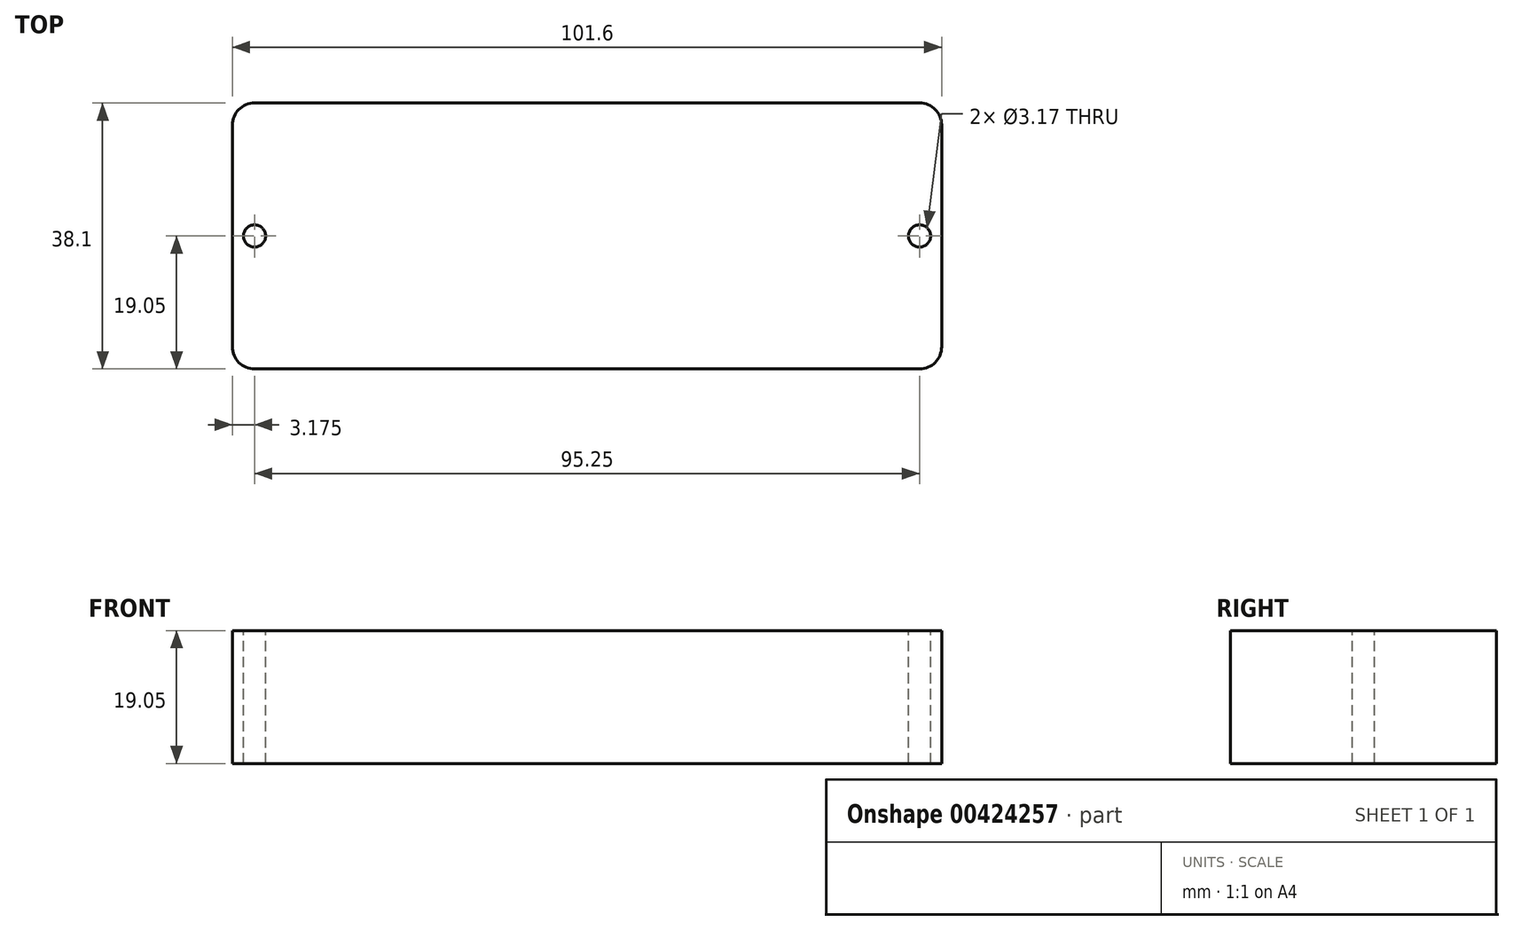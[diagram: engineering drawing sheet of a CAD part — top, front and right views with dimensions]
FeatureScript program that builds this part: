
annotation { "Feature Type Name" : "Feature", "Feature Type Description" : "" }
export const myFeature = defineFeature(function(context is Context, id is Id, definition is map)
    precondition{}
    {
        {
            var Q0;
            Q0=qCreatedBy(makeId("Top.planeOp"),FACE);
            var sketch = newSketch(context, id + "F0", { "sketchPlane" : qUnion([Q0])});
            skLineSegment(sketch, "E0.bottom", {"start": v(-50.8, -19.05) * mm, "end": v(50.8, -19.05) * mm});
            skLineSegment(sketch, "E0.top", {"start": v(-50.8, 19.05) * mm, "end": v(50.8, 19.05) * mm});
            skLineSegment(sketch, "E0.left", {"start": v(-50.8, -19.05) * mm, "end": v(-50.8, 19.05) * mm});
            skLineSegment(sketch, "E0.right", {"start": v(50.8, -19.05) * mm, "end": v(50.8, 19.05) * mm});
            skPoint(sketch, "E0.middle", {"position": v(0, 0) * mm});
            skSolve(sketch);
        }
        {
            var Q0;
            Q0=makeQuery(id+"F0.imprint","IMPRINT",FACE,{"disambiguationData":[TD([[makeQuery(id+"F0.imprint","IMPRINT",EDGE,{"derivedFrom":sQuery(id+"F0.wireOp",EDGE,"E0.bottom")}),1.0]])]});
            extrude(context, id + "F1", {"entities" : qUnion([Q0]), "depth" : 19.05 * mm});
        }
        {
            var Q0;
            Q0=makeQuery(id+"F1.opExtrude","SWEPT_EDGE",EDGE,{"disambiguationData":[OSD([sQuery(id+"F0.wireOp",EDGE,"E0.top"),sQuery(id+"F0.wireOp",EDGE,"E0.left")])]});
            var Q1;
            Q1=makeQuery(id+"F1.opExtrude","SWEPT_EDGE",EDGE,{"disambiguationData":[OSD([sQuery(id+"F0.wireOp",EDGE,"E0.bottom"),sQuery(id+"F0.wireOp",EDGE,"E0.left")])]});
            var Q2;
            Q2=makeQuery(id+"F1.opExtrude","SWEPT_EDGE",EDGE,{"disambiguationData":[OSD([sQuery(id+"F0.wireOp",EDGE,"E0.top"),sQuery(id+"F0.wireOp",EDGE,"E0.right")])]});
            var Q3;
            Q3=makeQuery(id+"F1.opExtrude","SWEPT_EDGE",EDGE,{"disambiguationData":[OSD([sQuery(id+"F0.wireOp",EDGE,"E0.bottom"),sQuery(id+"F0.wireOp",EDGE,"E0.right")])]});
            fillet(context, id + "F2", {"entities" : qUnion([Q0, Q1, Q2, Q3]), "radius" : 3.17 * mm, "tangentPropagation" : true, "allowEdgeOverflow" : false});
        }
        {
            var Q0;
            Q0=makeQuery(id+"F1.opExtrude","CAP_FACE",FACE,{"disambiguationData":[OSD([sQuery(id+"F0.wireOp",EDGE,"E0.bottom"),sQuery(id+"F0.wireOp",EDGE,"E0.top"),sQuery(id+"F0.wireOp",EDGE,"E0.left"),sQuery(id+"F0.wireOp",EDGE,"E0.right")])],"isStart":false});
            var sketch = newSketch(context, id + "F3", { "sketchPlane" : qUnion([Q0])});
            skLineSegment(sketch, "E1", {"start": v(0, 0) * mm, "end": v(-47.63, 0) * mm});
            skLineSegment(sketch, "E2", {"start": v(0, 0) * mm, "end": v(47.63, 0) * mm});
            skSolve(sketch);
        }
        {
            var Q0;
            Q0=sQuery(id+"F3.wireOp",VERTEX,"E1.end");
            var Q1;
            Q1=sQuery(id+"F3.wireOp",VERTEX,"E2.end");
            var Q2;
            Q2=makeQuery(id+"F1.opExtrude","SWEPT_BODY",BODY,{"disambiguationData":[OSD([sQuery(id+"F0.wireOp",EDGE,"E0.bottom"),sQuery(id+"F0.wireOp",EDGE,"E0.top"),sQuery(id+"F0.wireOp",EDGE,"E0.left"),sQuery(id+"F0.wireOp",EDGE,"E0.right")])]});
            hole(context, id + "F4", {"style" : HoleStyle.SIMPLE, "endStyle" : HoleEndStyle.THROUGH, "holeDiameter" : 3.17 * mm, "isTappedThrough" : true, "tappedDepth" : 12.7 * mm, "tapClearance" : 3, "locations" : qUnion([Q0, Q1]), "scope" : qUnion([Q2])});
        }
    });
